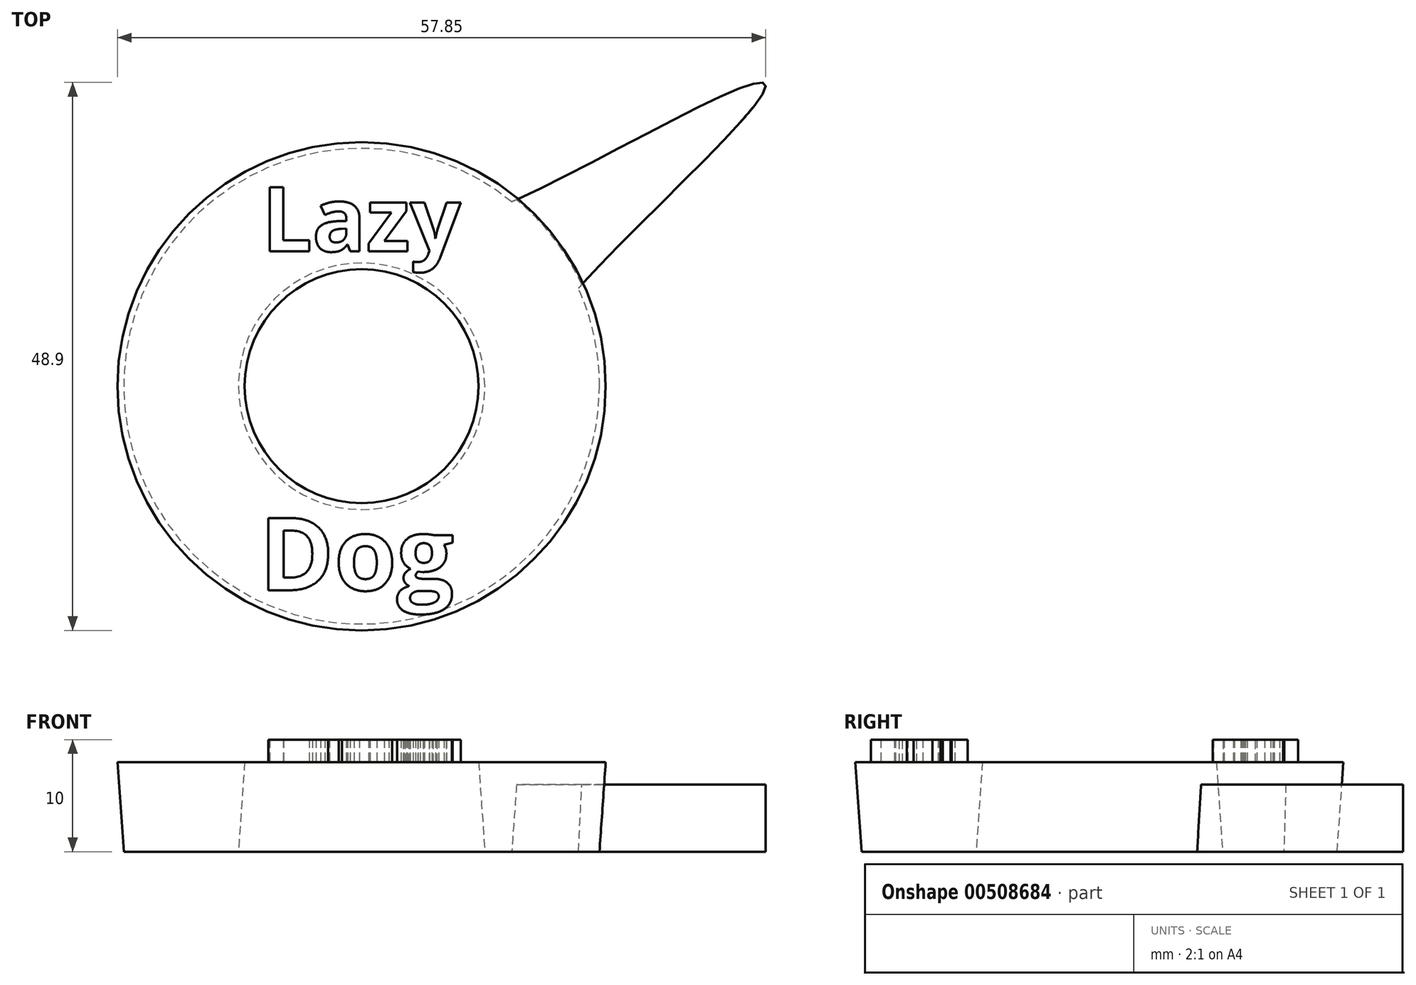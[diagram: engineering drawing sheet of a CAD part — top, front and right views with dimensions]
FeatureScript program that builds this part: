
annotation { "Feature Type Name" : "Feature", "Feature Type Description" : "" }
export const myFeature = defineFeature(function(context is Context, id is Id, definition is map)
    precondition{}
    {
        {
            var Q0;
            Q0=qCreatedBy(makeId("Top.planeOp"),FACE);
            var sketch = newSketch(context, id + "F0", { "sketchPlane" : qUnion([Q0])});
            skCircle(sketch, "E0", {"center": v(0, 0) * mm, "radius": 21.23 * mm});
            skCircle(sketch, "E1", {"center": v(0, 0) * mm, "radius": 11 * mm});
            skFitSpline(sketch, "E2", {"points": [v(13.4, 16.46) * mm, v(36.01, 26.98) * mm, v(19.35, 8.73) * mm], "startDerivative": vector(40.22, 17.03) * mm, "endDerivative": vector(-28.43, -32.6) * mm});
            skSolve(sketch);
        }
        {
            var Q0;
            Q0=makeQuery(id+"F0.imprint","IMPRINT",FACE,{"disambiguationData":[TD([[makeQuery(id+"F0.imprint","IMPRINT",EDGE,{"derivedFrom":sQuery(id+"F0.wireOp",EDGE,"E0")}),1.0]])]});
            extrude(context, id + "F1", {"entities" : qUnion([Q0]), "depth" : 8 * mm, "hasDraft" : true, "draftAngle" : 4 * degree});
        }
        {
            var Q0;
            {var subQ0=sQuery(id+"F0.wireOp",EDGE,"E2");Q0=makeQuery(id+"F0.imprint","IMPRINT",FACE,{"disambiguationData":[TD([[makeQuery(id+"F0.imprint","IMPRINT",EDGE,{"derivedFrom":subQ0}),-1.0]])]});}
            extrude(context, id + "F2", {"entities" : qUnion([Q0]), "operationType" : NewBodyOperationType.ADD, "depth" : 6 * mm});
        }
        {
            var Q0;
            Q0=makeQuery(id+"F1.opExtrude","CAP_FACE",FACE,{"disambiguationData":[OSD([sQuery(id+"F0.wireOp",EDGE,"E0"),sQuery(id+"F0.wireOp",EDGE,"E1")])],"isStart":false});
            var sketch = newSketch(context, id + "F3", { "sketchPlane" : qUnion([Q0])});
            skText(sketch, "E3", { "text": "Lazy", "fontName": "OpenSans-Bold.ttf"});
            skText(sketch, "E4", { "text": "Dog", "fontName": "OpenSans-Bold.ttf"});
            const initialGuessF3  = {"E3": [-0.00892, 0.01204, 1, 0, 0.00575], "E4": [-0.00914, -0.01821, 1, 0, 0.0065]};
            skSetInitialGuess(sketch, initialGuessF3);
            skSolve(sketch);
        }
        {
            var Q0;
            Q0 = qSketchRegion(id + "F3", true);
            extrude(context, id + "F4", {"entities" : qUnion([Q0]), "operationType" : NewBodyOperationType.ADD, "depth" : 2 * mm});
        }
    });
